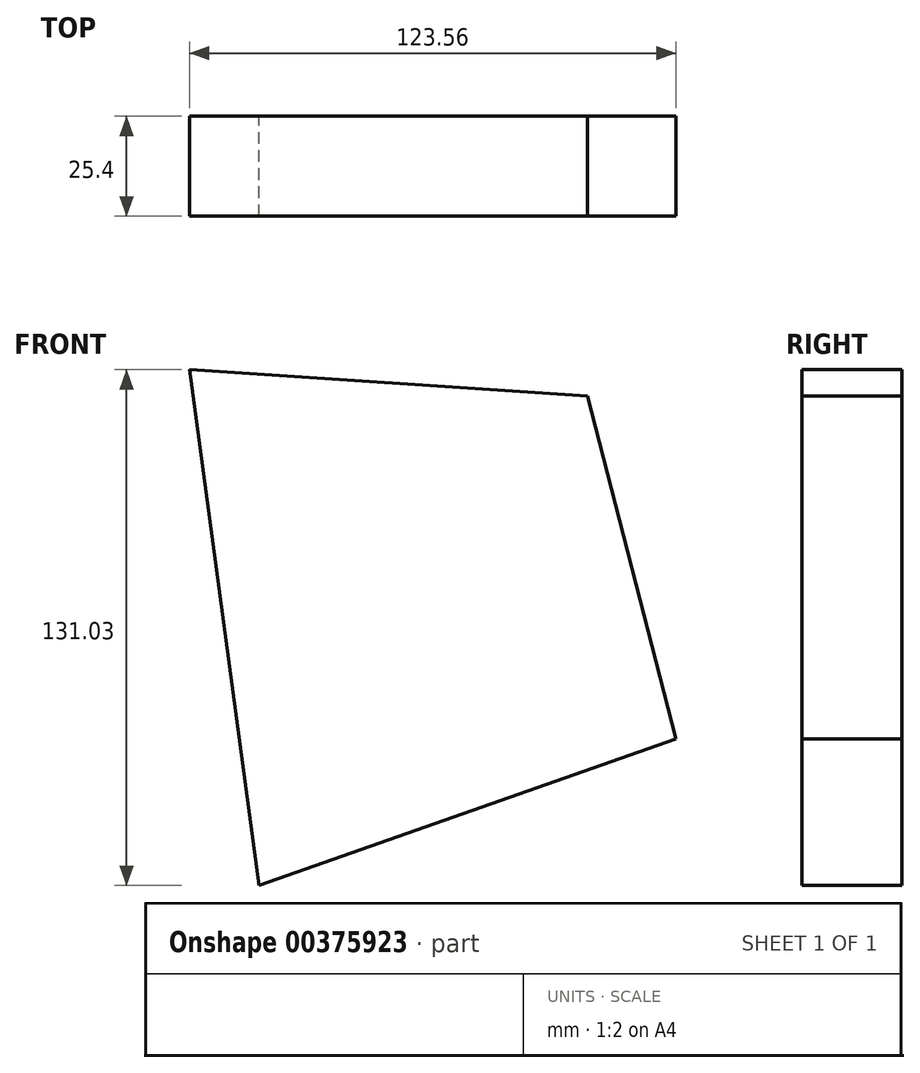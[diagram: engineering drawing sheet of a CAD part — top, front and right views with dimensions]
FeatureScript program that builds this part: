
annotation { "Feature Type Name" : "Feature", "Feature Type Description" : "" }
export const myFeature = defineFeature(function(context is Context, id is Id, definition is map)
    precondition{}
    {
        {
            var Q0;
            Q0=qCreatedBy(makeId("Front.planeOp"),FACE);
            var sketch = newSketch(context, id + "F0", { "sketchPlane" : qUnion([Q0])});
            skLineSegment(sketch, "E0", {"start": v(-51.26, 118.29) * mm, "end": v(-33.57, -12.74) * mm});
            skLineSegment(sketch, "E1", {"start": v(-33.57, -12.74) * mm, "end": v(72.3, 24.5) * mm});
            skLineSegment(sketch, "E2", {"start": v(72.3, 24.5) * mm, "end": v(49.83, 111.61) * mm});
            skLineSegment(sketch, "E3", {"start": v(49.83, 111.61) * mm, "end": v(-51.26, 118.29) * mm});
            skSolve(sketch);
        }
        {
            var Q0;
            Q0 = qSketchRegion(id + "F0", true);
            extrude(context, id + "F1", {"entities" : qUnion([Q0]), "depth" : 25.4 * mm});
        }
    });
